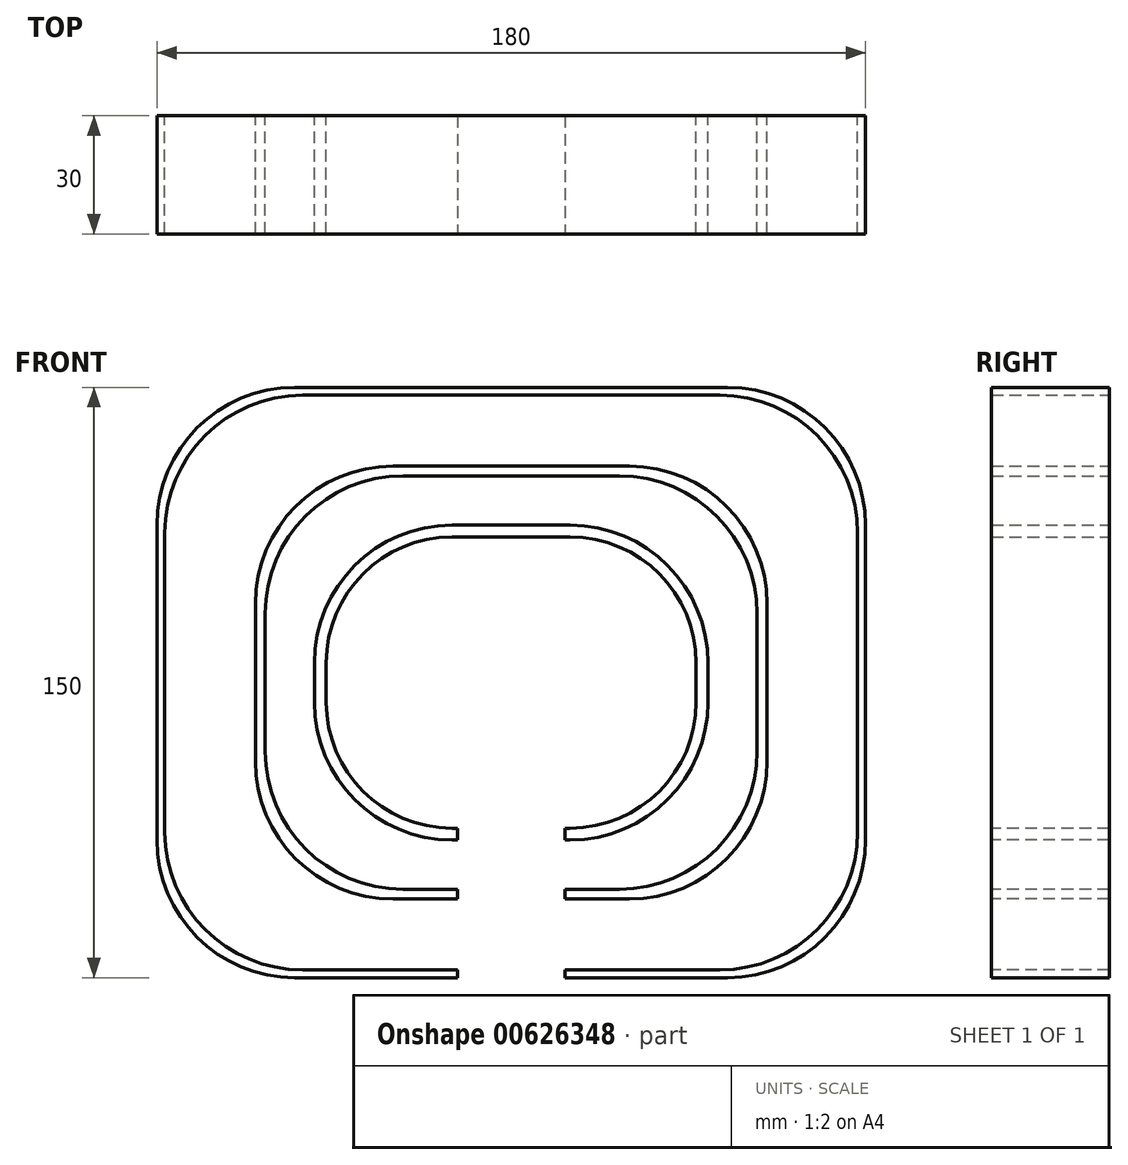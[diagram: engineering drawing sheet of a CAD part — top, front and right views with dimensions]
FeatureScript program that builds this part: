
annotation { "Feature Type Name" : "Feature", "Feature Type Description" : "" }
export const myFeature = defineFeature(function(context is Context, id is Id, definition is map)
    precondition{}
    {
        {
            var Q0;
            Q0=qCreatedBy(makeId("Front.planeOp"),FACE);
            var sketch = newSketch(context, id + "F0", { "sketchPlane" : qUnion([Q0])});
            skLineSegment(sketch, "E0.bottom", {"start": v(90, 75) * mm, "end": v(-90, 75) * mm});
            skLineSegment(sketch, "E0.top", {"start": v(90, -75) * mm, "end": v(-90, -75) * mm});
            skLineSegment(sketch, "E0.left", {"start": v(90, 75) * mm, "end": v(90, -75) * mm});
            skLineSegment(sketch, "E0.right", {"start": v(-90, 75) * mm, "end": v(-90, -75) * mm});
            skPoint(sketch, "E0.middle", {"position": v(0, 0) * mm});
            skSolve(sketch);
        }
        {
            var Q0;
            Q0 = qSketchRegion(id + "F0", true);
            extrude(context, id + "F1", {"entities" : qUnion([Q0]), "depth" : 30 * mm, "offsetDistance" : 25 * mm});
        }
        {
            var Q0;
            Q0=makeQuery(id+"F1.opExtrude","CAP_FACE",FACE,{"disambiguationData":[OSD([sQuery(id+"F0.wireOp",EDGE,"E0.bottom"),sQuery(id+"F0.wireOp",EDGE,"E0.top"),sQuery(id+"F0.wireOp",EDGE,"E0.left"),sQuery(id+"F0.wireOp",EDGE,"E0.right")])],"isStart":false});
            var Q1;
            Q1=makeQuery(id+"F1.opExtrude","CAP_FACE",FACE,{"disambiguationData":[OSD([sQuery(id+"F0.wireOp",EDGE,"E0.bottom"),sQuery(id+"F0.wireOp",EDGE,"E0.top"),sQuery(id+"F0.wireOp",EDGE,"E0.left"),sQuery(id+"F0.wireOp",EDGE,"E0.right")])],"isStart":true});
            shell(context, id + "F2", {"entities" : qUnion([Q0, Q1]), "thickness" : 2 * mm});
        }
        {
            var Q0;
            Q0=makeQuery(id+"F0.imprint","IMPRINT",FACE,{"disambiguationData":[TD([[makeQuery(id+"F0.imprint","IMPRINT",EDGE,{"derivedFrom":sQuery(id+"F0.wireOp",EDGE,"E0.bottom")}),1.0]])]});
            var sketch = newSketch(context, id + "F3", { "sketchPlane" : qUnion([Q0])});
            skLineSegment(sketch, "E1.bottom", {"start": v(65, 55) * mm, "end": v(-65, 55) * mm});
            skLineSegment(sketch, "E1.top", {"start": v(65, -55) * mm, "end": v(-65, -55) * mm});
            skLineSegment(sketch, "E1.left", {"start": v(65, 55) * mm, "end": v(65, -55) * mm});
            skLineSegment(sketch, "E1.right", {"start": v(-65, 55) * mm, "end": v(-65, -55) * mm});
            skPoint(sketch, "E1.middle", {"position": v(0, 0) * mm});
            skSolve(sketch);
        }
        {
            var Q0;
            Q0 = qSketchRegion(id + "F3", true);
            extrude(context, id + "F4", {"entities" : qUnion([Q0]), "depth" : 30 * mm, "offsetDistance" : 25 * mm});
        }
        {
            var Q0;
            Q0=makeQuery(id+"F4.opExtrude","CAP_FACE",FACE,{"disambiguationData":[OSD([sQuery(id+"F3.wireOp",EDGE,"E1.bottom"),sQuery(id+"F3.wireOp",EDGE,"E1.top"),sQuery(id+"F3.wireOp",EDGE,"E1.left"),sQuery(id+"F3.wireOp",EDGE,"E1.right")])],"isStart":false});
            var Q1;
            Q1=makeQuery(id+"F4.opExtrude","CAP_FACE",FACE,{"disambiguationData":[OSD([sQuery(id+"F3.wireOp",EDGE,"E1.bottom"),sQuery(id+"F3.wireOp",EDGE,"E1.top"),sQuery(id+"F3.wireOp",EDGE,"E1.left"),sQuery(id+"F3.wireOp",EDGE,"E1.right")])],"isStart":true});
            shell(context, id + "F5", {"entities" : qUnion([Q0, Q1]), "thickness" : 2.5 * mm});
        }
        {
            var Q0;
            Q0=makeQuery(id+"F0.imprint","IMPRINT",FACE,{"disambiguationData":[TD([[makeQuery(id+"F0.imprint","IMPRINT",EDGE,{"derivedFrom":sQuery(id+"F0.wireOp",EDGE,"E0.bottom")}),1.0]])]});
            var sketch = newSketch(context, id + "F6", { "sketchPlane" : qUnion([Q0])});
            skLineSegment(sketch, "E2.bottom", {"start": v(50, 40) * mm, "end": v(-50, 40) * mm});
            skLineSegment(sketch, "E2.top", {"start": v(50, -40) * mm, "end": v(-50, -40) * mm});
            skLineSegment(sketch, "E2.left", {"start": v(50, 40) * mm, "end": v(50, -40) * mm});
            skLineSegment(sketch, "E2.right", {"start": v(-50, 40) * mm, "end": v(-50, -40) * mm});
            skPoint(sketch, "E2.middle", {"position": v(0, 0) * mm});
            skSolve(sketch);
        }
        {
            var Q0;
            Q0 = qSketchRegion(id + "F6", true);
            extrude(context, id + "F7", {"entities" : qUnion([Q0]), "depth" : 30 * mm, "offsetDistance" : 25 * mm});
        }
        {
            var Q0;
            Q0=makeQuery(id+"F7.opExtrude","SWEPT_EDGE",EDGE,{"disambiguationData":[OSD([sQuery(id+"F6.wireOp",EDGE,"E2.bottom"),sQuery(id+"F6.wireOp",EDGE,"E2.left")])]});
            var Q1;
            Q1=makeQuery(id+"F9.opShell","OFFSET_EDGE",EDGE,{"disambiguationData":[OSD([sQuery(id+"F6.wireOp",EDGE,"E2.bottom"),sQuery(id+"F6.wireOp",EDGE,"E2.left")])]});
            var Q2;
            Q2=makeQuery(id+"F7.opExtrude","SWEPT_EDGE",EDGE,{"disambiguationData":[OSD([sQuery(id+"F6.wireOp",EDGE,"E2.bottom"),sQuery(id+"F6.wireOp",EDGE,"E2.right")])]});
            var Q3;
            Q3=makeQuery(id+"F9.opShell","OFFSET_EDGE",EDGE,{"disambiguationData":[OSD([sQuery(id+"F6.wireOp",EDGE,"E2.bottom"),sQuery(id+"F6.wireOp",EDGE,"E2.right")])]});
            var Q4;
            Q4=makeQuery(id+"F9.opShell","OFFSET_EDGE",EDGE,{"disambiguationData":[OSD([sQuery(id+"F6.wireOp",EDGE,"E2.top"),sQuery(id+"F6.wireOp",EDGE,"E2.right")])]});
            var Q5;
            Q5=makeQuery(id+"F7.opExtrude","SWEPT_EDGE",EDGE,{"disambiguationData":[OSD([sQuery(id+"F6.wireOp",EDGE,"E2.top"),sQuery(id+"F6.wireOp",EDGE,"E2.right")])]});
            var Q6;
            Q6=makeQuery(id+"F7.opExtrude","SWEPT_EDGE",EDGE,{"disambiguationData":[OSD([sQuery(id+"F6.wireOp",EDGE,"E2.top"),sQuery(id+"F6.wireOp",EDGE,"E2.left")])]});
            var Q7;
            Q7=makeQuery(id+"F9.opShell","OFFSET_EDGE",EDGE,{"disambiguationData":[OSD([sQuery(id+"F6.wireOp",EDGE,"E2.top"),sQuery(id+"F6.wireOp",EDGE,"E2.left")])]});
            var Q8;
            Q8=makeQuery(id+"F5.opShell","OFFSET_EDGE",EDGE,{"disambiguationData":[OSD([sQuery(id+"F3.wireOp",EDGE,"E1.bottom"),sQuery(id+"F3.wireOp",EDGE,"E1.right")])]});
            var Q9;
            Q9=makeQuery(id+"F4.opExtrude","SWEPT_EDGE",EDGE,{"disambiguationData":[OSD([sQuery(id+"F3.wireOp",EDGE,"E1.bottom"),sQuery(id+"F3.wireOp",EDGE,"E1.right")])]});
            var Q10;
            Q10=makeQuery(id+"F5.opShell","OFFSET_EDGE",EDGE,{"disambiguationData":[OSD([sQuery(id+"F3.wireOp",EDGE,"E1.top"),sQuery(id+"F3.wireOp",EDGE,"E1.right")])]});
            var Q11;
            Q11=makeQuery(id+"F4.opExtrude","SWEPT_EDGE",EDGE,{"disambiguationData":[OSD([sQuery(id+"F3.wireOp",EDGE,"E1.top"),sQuery(id+"F3.wireOp",EDGE,"E1.right")])]});
            var Q12;
            Q12=makeQuery(id+"F2.opShell","OFFSET_EDGE",EDGE,{"disambiguationData":[OSD([sQuery(id+"F0.wireOp",EDGE,"E0.bottom"),sQuery(id+"F0.wireOp",EDGE,"E0.right")])]});
            var Q13;
            Q13=makeQuery(id+"F1.opExtrude","SWEPT_EDGE",EDGE,{"disambiguationData":[OSD([sQuery(id+"F0.wireOp",EDGE,"E0.bottom"),sQuery(id+"F0.wireOp",EDGE,"E0.right")])]});
            var Q14;
            Q14=makeQuery(id+"F1.opExtrude","SWEPT_EDGE",EDGE,{"disambiguationData":[OSD([sQuery(id+"F0.wireOp",EDGE,"E0.bottom"),sQuery(id+"F0.wireOp",EDGE,"E0.left")])]});
            var Q15;
            Q15=makeQuery(id+"F2.opShell","OFFSET_EDGE",EDGE,{"disambiguationData":[OSD([sQuery(id+"F0.wireOp",EDGE,"E0.bottom"),sQuery(id+"F0.wireOp",EDGE,"E0.left")])]});
            var Q16;
            Q16=makeQuery(id+"F5.opShell","OFFSET_EDGE",EDGE,{"disambiguationData":[OSD([sQuery(id+"F3.wireOp",EDGE,"E1.top"),sQuery(id+"F3.wireOp",EDGE,"E1.left")])]});
            var Q17;
            Q17=makeQuery(id+"F2.opShell","OFFSET_EDGE",EDGE,{"disambiguationData":[OSD([sQuery(id+"F0.wireOp",EDGE,"E0.top"),sQuery(id+"F0.wireOp",EDGE,"E0.left")])]});
            var Q18;
            Q18=makeQuery(id+"F5.opShell","OFFSET_EDGE",EDGE,{"disambiguationData":[OSD([sQuery(id+"F3.wireOp",EDGE,"E1.bottom"),sQuery(id+"F3.wireOp",EDGE,"E1.left")])]});
            var Q19;
            Q19=makeQuery(id+"F4.opExtrude","SWEPT_EDGE",EDGE,{"disambiguationData":[OSD([sQuery(id+"F3.wireOp",EDGE,"E1.top"),sQuery(id+"F3.wireOp",EDGE,"E1.left")])]});
            var Q20;
            Q20=makeQuery(id+"F1.opExtrude","SWEPT_EDGE",EDGE,{"disambiguationData":[OSD([sQuery(id+"F0.wireOp",EDGE,"E0.top"),sQuery(id+"F0.wireOp",EDGE,"E0.left")])]});
            var Q21;
            Q21=makeQuery(id+"F4.opExtrude","SWEPT_EDGE",EDGE,{"disambiguationData":[OSD([sQuery(id+"F3.wireOp",EDGE,"E1.bottom"),sQuery(id+"F3.wireOp",EDGE,"E1.left")])]});
            var Q22;
            Q22=makeQuery(id+"F2.opShell","OFFSET_EDGE",EDGE,{"disambiguationData":[OSD([sQuery(id+"F0.wireOp",EDGE,"E0.top"),sQuery(id+"F0.wireOp",EDGE,"E0.right")])]});
            var Q23;
            Q23=makeQuery(id+"F1.opExtrude","SWEPT_EDGE",EDGE,{"disambiguationData":[OSD([sQuery(id+"F0.wireOp",EDGE,"E0.top"),sQuery(id+"F0.wireOp",EDGE,"E0.right")])]});
            fillet(context, id + "F8", {"entities" : qUnion([Q0, Q1, Q2, Q3, Q4, Q5, Q6, Q7, Q8, Q9, Q10, Q11, Q12, Q13, Q14, Q15, Q16, Q17, Q18, Q19, Q20, Q21, Q22, Q23]), "radius" : 35 * mm, "tangentPropagation" : true, "allowEdgeOverflow" : false});
        }
        {
            var Q0;
            Q0=makeQuery(id+"F7.opExtrude","CAP_FACE",FACE,{"disambiguationData":[OSD([sQuery(id+"F6.wireOp",EDGE,"E2.bottom"),sQuery(id+"F6.wireOp",EDGE,"E2.top"),sQuery(id+"F6.wireOp",EDGE,"E2.left"),sQuery(id+"F6.wireOp",EDGE,"E2.right")])],"isStart":false});
            var Q1;
            Q1=makeQuery(id+"F7.opExtrude","CAP_FACE",FACE,{"disambiguationData":[OSD([sQuery(id+"F6.wireOp",EDGE,"E2.bottom"),sQuery(id+"F6.wireOp",EDGE,"E2.top"),sQuery(id+"F6.wireOp",EDGE,"E2.left"),sQuery(id+"F6.wireOp",EDGE,"E2.right")])],"isStart":true});
            shell(context, id + "F9", {"entities" : qUnion([Q0, Q1]), "thickness" : 3 * mm});
        }
        {
            var Q0;
            Q0=makeQuery(id+"F0.imprint","IMPRINT",FACE,{"disambiguationData":[TD([[makeQuery(id+"F0.imprint","IMPRINT",EDGE,{"derivedFrom":sQuery(id+"F0.wireOp",EDGE,"E0.bottom")}),1.0]])]});
            var sketch = newSketch(context, id + "F10", { "sketchPlane" : qUnion([Q0])});
            skLineSegment(sketch, "E3.bottom", {"start": v(-13.69, -33.46) * mm, "end": v(13.69, -33.46) * mm});
            skLineSegment(sketch, "E3.top", {"start": v(-13.69, -124.7) * mm, "end": v(13.69, -124.7) * mm});
            skLineSegment(sketch, "E3.left", {"start": v(-13.69, -33.46) * mm, "end": v(-13.69, -124.7) * mm});
            skLineSegment(sketch, "E3.right", {"start": v(13.69, -33.46) * mm, "end": v(13.69, -124.7) * mm});
            skSolve(sketch);
        }
        {
            var Q0;
            Q0 = qSketchRegion(id + "F10", true);
            extrude(context, id + "F11", {"entities" : qUnion([Q0]), "operationType" : NewBodyOperationType.REMOVE, "endBound" : BoundingType.THROUGH_ALL, "depth" : 25 * mm, "offsetDistance" : 25 * mm});
        }
    });
